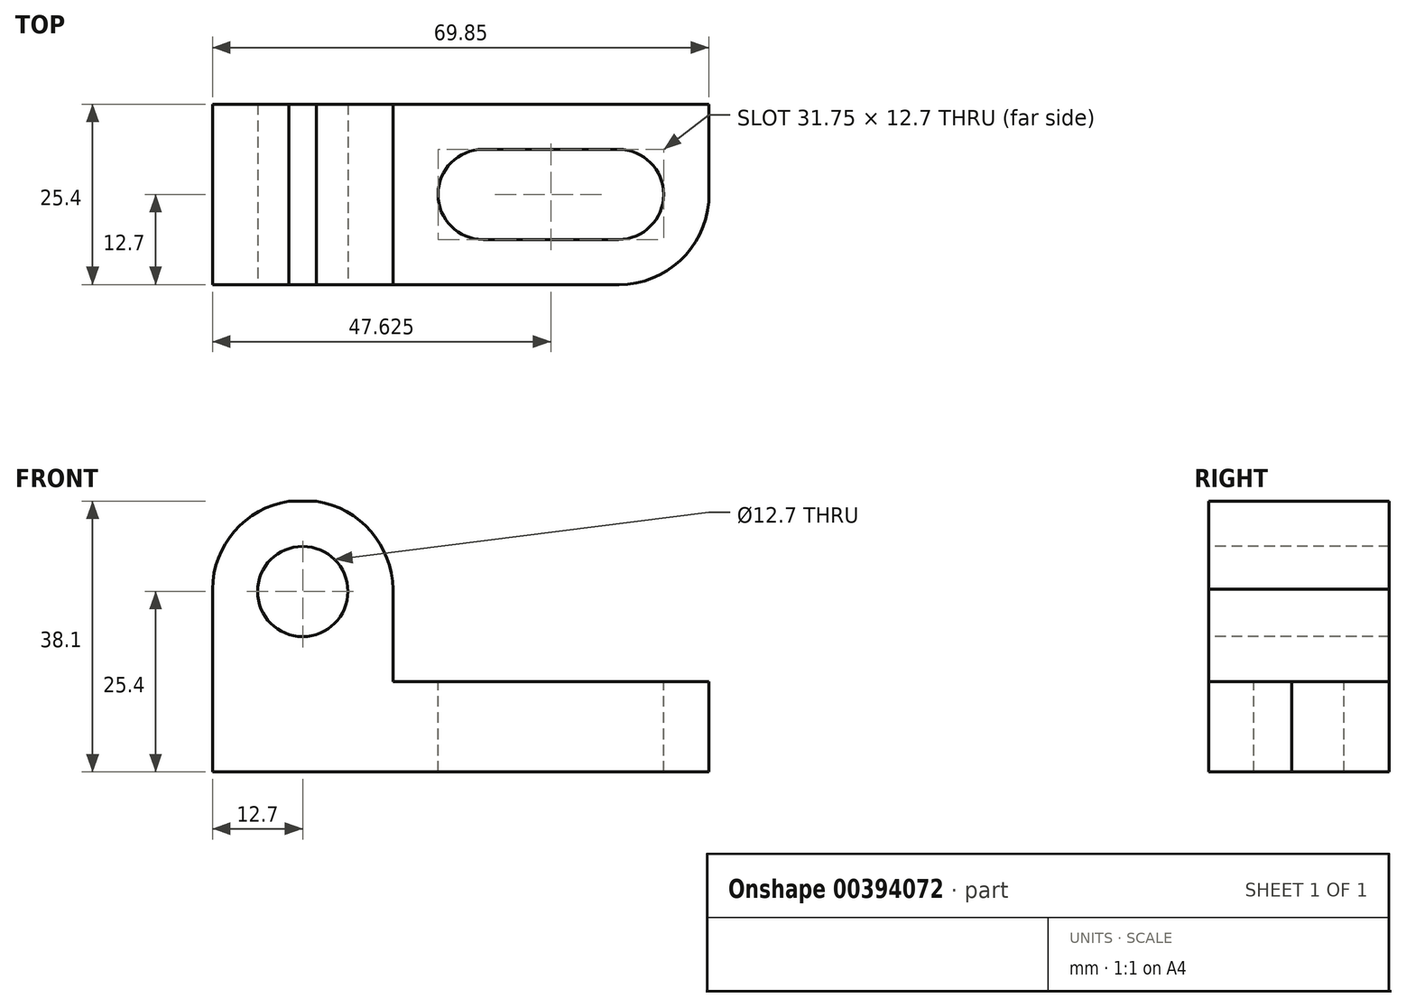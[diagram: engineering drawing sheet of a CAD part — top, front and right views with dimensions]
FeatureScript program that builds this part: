
annotation { "Feature Type Name" : "Feature", "Feature Type Description" : "" }
export const myFeature = defineFeature(function(context is Context, id is Id, definition is map)
    precondition{}
    {
        {
            var Q0;
            Q0=qCreatedBy(makeId("Front.planeOp"),FACE);
            var sketch = newSketch(context, id + "F0", { "sketchPlane" : qUnion([Q0])});
            skLineSegment(sketch, "E0", {"start": v(0, 0) * mm, "end": v(0, 38.1) * mm});
            skLineSegment(sketch, "E1", {"start": v(0, 38.1) * mm, "end": v(25.4, 38.1) * mm});
            skLineSegment(sketch, "E2", {"start": v(25.4, 38.1) * mm, "end": v(25.4, 12.7) * mm});
            skLineSegment(sketch, "E3", {"start": v(25.4, 12.7) * mm, "end": v(69.85, 12.7) * mm});
            skLineSegment(sketch, "E4", {"start": v(69.85, 12.7) * mm, "end": v(69.85, 0) * mm});
            skLineSegment(sketch, "E5", {"start": v(69.85, 0) * mm, "end": v(0, 0) * mm});
            skSolve(sketch);
        }
        {
            var Q0;
            Q0=makeQuery(id+"F0.imprint","IMPRINT",FACE,{"disambiguationData":[TD([[makeQuery(id+"F0.imprint","IMPRINT",EDGE,{"derivedFrom":sQuery(id+"F0.wireOp",EDGE,"E0")}),-1.0]])]});
            extrude(context, id + "F1", {"entities" : qUnion([Q0]), "depth" : 25.4 * mm});
        }
        {
            var Q0;
            Q0=makeQuery(id+"F1.opExtrude","CAP_FACE",FACE,{"disambiguationData":[OSD([sQuery(id+"F0.wireOp",EDGE,"E0"),sQuery(id+"F0.wireOp",EDGE,"E1"),sQuery(id+"F0.wireOp",EDGE,"E2"),sQuery(id+"F0.wireOp",EDGE,"E3"),sQuery(id+"F0.wireOp",EDGE,"E4"),sQuery(id+"F0.wireOp",EDGE,"E5")])],"isStart":false});
            var sketch = newSketch(context, id + "F2", { "sketchPlane" : qUnion([Q0])});
            skCircle(sketch, "E6", {"center": v(12.7, 25.4) * mm, "radius": 6.35 * mm});
            skArc(sketch, "E7", {"start": v(25.4, 25.4) * mm, "mid": v(12.7, 38.25) * mm, "end": v(0, 25.4) * mm});
            skSolve(sketch);
        }
        {
            var Q0;
            Q0=makeQuery(id+"F2.imprint","IMPRINT",FACE,{"disambiguationData":[TD([[makeQuery(id+"F2.imprint","IMPRINT",EDGE,{"derivedFrom":sQuery(id+"F2.wireOp",EDGE,"E6")}),1.0]])]});
            var Q1;
            {var subQ0=sQuery(id+"F2.wireOp",EDGE,"E7");var subQ1=makeQuery(id+"F1.opExtrude","CAP_EDGE",EDGE,{"disambiguationData":[OSD([sQuery(id+"F0.wireOp",EDGE,"E1")])],"isStart":false});var subQ2=makeQuery(id+"F2.imprint","INTERSECT",VERTEX,{"disambiguationData":[OD(1.0)],"derivedFrom":[subQ1,subQ0]});Q1=makeQuery(id+"F2.imprint","IMPRINT",FACE,{"disambiguationData":[TD([[makeQuery(id+"F2.imprint","IMPRINT",EDGE,{"disambiguationData":[TD([[subQ2,-1.0]])],"derivedFrom":subQ0}),-1.0]])]});}
            var Q2;
            {var subQ0=sQuery(id+"F2.wireOp",EDGE,"E7");var subQ1=makeQuery(id+"F1.opExtrude","CAP_EDGE",EDGE,{"disambiguationData":[OSD([sQuery(id+"F0.wireOp",EDGE,"E2")])],"isStart":false});var subQ2=makeQuery(id+"F2.imprint","INTERSECT",VERTEX,{"disambiguationData":[OD(1.0)],"derivedFrom":[subQ1,subQ0]});Q2=makeQuery(id+"F2.imprint","IMPRINT",FACE,{"disambiguationData":[TD([[makeQuery(id+"F2.imprint","IMPRINT",EDGE,{"disambiguationData":[TD([[subQ2,-1.0]])],"derivedFrom":subQ0}),-1.0]])]});}
            extrude(context, id + "F3", {"entities" : qUnion([Q0, Q1, Q2]), "operationType" : NewBodyOperationType.REMOVE, "oppositeDirection" : true, "depth" : 25.4 * mm});
        }
        {
            var Q0;
            Q0=makeQuery(id+"F1.opExtrude","SWEPT_FACE",FACE,{"disambiguationData":[OSD([sQuery(id+"F0.wireOp",EDGE,"E3")])]});
            var sketch = newSketch(context, id + "F4", { "sketchPlane" : qUnion([Q0])});
            skCircle(sketch, "E8", {"center": v(38.1, -12.7) * mm, "radius": 6.35 * mm});
            skCircle(sketch, "E9", {"center": v(57.15, -12.7) * mm, "radius": 6.35 * mm});
            skLineSegment(sketch, "E10", {"start": v(38.1, -6.35) * mm, "end": v(57.15, -6.35) * mm});
            skLineSegment(sketch, "E11", {"start": v(57.15, -6.35) * mm, "end": v(57.15, -19.05) * mm});
            skLineSegment(sketch, "E12", {"start": v(57.15, -19.05) * mm, "end": v(38.1, -19.05) * mm});
            skArc(sketch, "E13", {"start": v(57.15, -25.4) * mm, "mid": v(69.9, -12.7) * mm, "end": v(57.15, 0) * mm});
            skSolve(sketch);
        }
        {
            var Q0;
            {var subQ0=sQuery(id+"F4.wireOp",EDGE,"E10");Q0=makeQuery(id+"F4.imprint","IMPRINT",FACE,{"disambiguationData":[TD([[makeQuery(id+"F4.imprint","IMPRINT",EDGE,{"derivedFrom":subQ0}),-1.0]])]});}
            var Q1;
            {var subQ0=sQuery(id+"F4.wireOp",EDGE,"E8");var subQ1=makeQuery(id+"F4.imprint","INTERSECT",VERTEX,{"derivedFrom":[subQ0,sQuery(id+"F4.wireOp",EDGE,"E10")]});Q1=makeQuery(id+"F4.imprint","IMPRINT",FACE,{"disambiguationData":[TD([[makeQuery(id+"F4.imprint","IMPRINT",EDGE,{"disambiguationData":[TD([[subQ1,-1.0]])],"derivedFrom":subQ0}),1.0]])]});}
            var Q2;
            {var subQ0=sQuery(id+"F4.wireOp",EDGE,"E11");Q2=makeQuery(id+"F4.imprint","IMPRINT",FACE,{"disambiguationData":[TD([[makeQuery(id+"F4.imprint","IMPRINT",EDGE,{"derivedFrom":subQ0}),-1.0]])]});}
            var Q3;
            {var subQ0=sQuery(id+"F4.wireOp",EDGE,"E11");Q3=makeQuery(id+"F4.imprint","IMPRINT",FACE,{"disambiguationData":[TD([[makeQuery(id+"F4.imprint","IMPRINT",EDGE,{"derivedFrom":subQ0}),1.0]])]});}
            extrude(context, id + "F5", {"entities" : qUnion([Q0, Q1, Q2, Q3]), "operationType" : NewBodyOperationType.REMOVE, "oppositeDirection" : true, "depth" : 6.35 * mm});
        }
        {
            var Q0;
            Q0 = qSketchRegion(id + "F4", true);
            var Q1;
            Q1=makeQuery(id+"F5.boolean.opBoolean","COPY",FACE,{"derivedFrom":makeQuery(id+"F5.opExtrude","CAP_FACE",FACE,{"disambiguationData":[OSD([sQuery(id+"F4.wireOp",EDGE,"E8"),sQuery(id+"F4.wireOp",EDGE,"E9"),sQuery(id+"F4.wireOp",EDGE,"E10"),sQuery(id+"F4.wireOp",EDGE,"E12")])],"isStart":false})});
            var Q2;
            {var subQ0=sQuery(id+"F4.wireOp",EDGE,"E13");var subQ1=sQuery(id+"F0.wireOp",EDGE,"E3");var subQ2=makeQuery(id+"F1.opExtrude","CAP_EDGE",EDGE,{"disambiguationData":[OSD([subQ1])],"isStart":false});var subQ3=makeQuery(id+"F4.imprint","INTERSECT",VERTEX,{"disambiguationData":[OD(1.0)],"derivedFrom":[subQ2,subQ0]});Q2=makeQuery(id+"F4.imprint","IMPRINT",FACE,{"disambiguationData":[TD([[makeQuery(id+"F4.imprint","IMPRINT",EDGE,{"disambiguationData":[TD([[subQ3,-1.0]])],"derivedFrom":subQ0}),-1.0]])]});}
            var Q3;
            {var subQ0=sQuery(id+"F4.wireOp",EDGE,"E13");var subQ1=sQuery(id+"F0.wireOp",EDGE,"E3");var subQ4=makeQuery(id+"F1.opExtrude","SWEPT_EDGE",EDGE,{"disambiguationData":[OSD([subQ1,sQuery(id+"F0.wireOp",EDGE,"E4")])]});var subQ5=makeQuery(id+"F4.imprint","INTERSECT",VERTEX,{"disambiguationData":[OD(1.0)],"derivedFrom":[subQ4,subQ0]});Q3=makeQuery(id+"F4.imprint","IMPRINT",FACE,{"disambiguationData":[TD([[makeQuery(id+"F4.imprint","IMPRINT",EDGE,{"disambiguationData":[TD([[subQ5,-1.0]])],"derivedFrom":subQ0}),-1.0]])]});}
            extrude(context, id + "F6", {"entities" : qUnion([Q0, Q1, Q2, Q3]), "operationType" : NewBodyOperationType.REMOVE, "oppositeDirection" : true, "depth" : 12.7 * mm});
        }
    });
